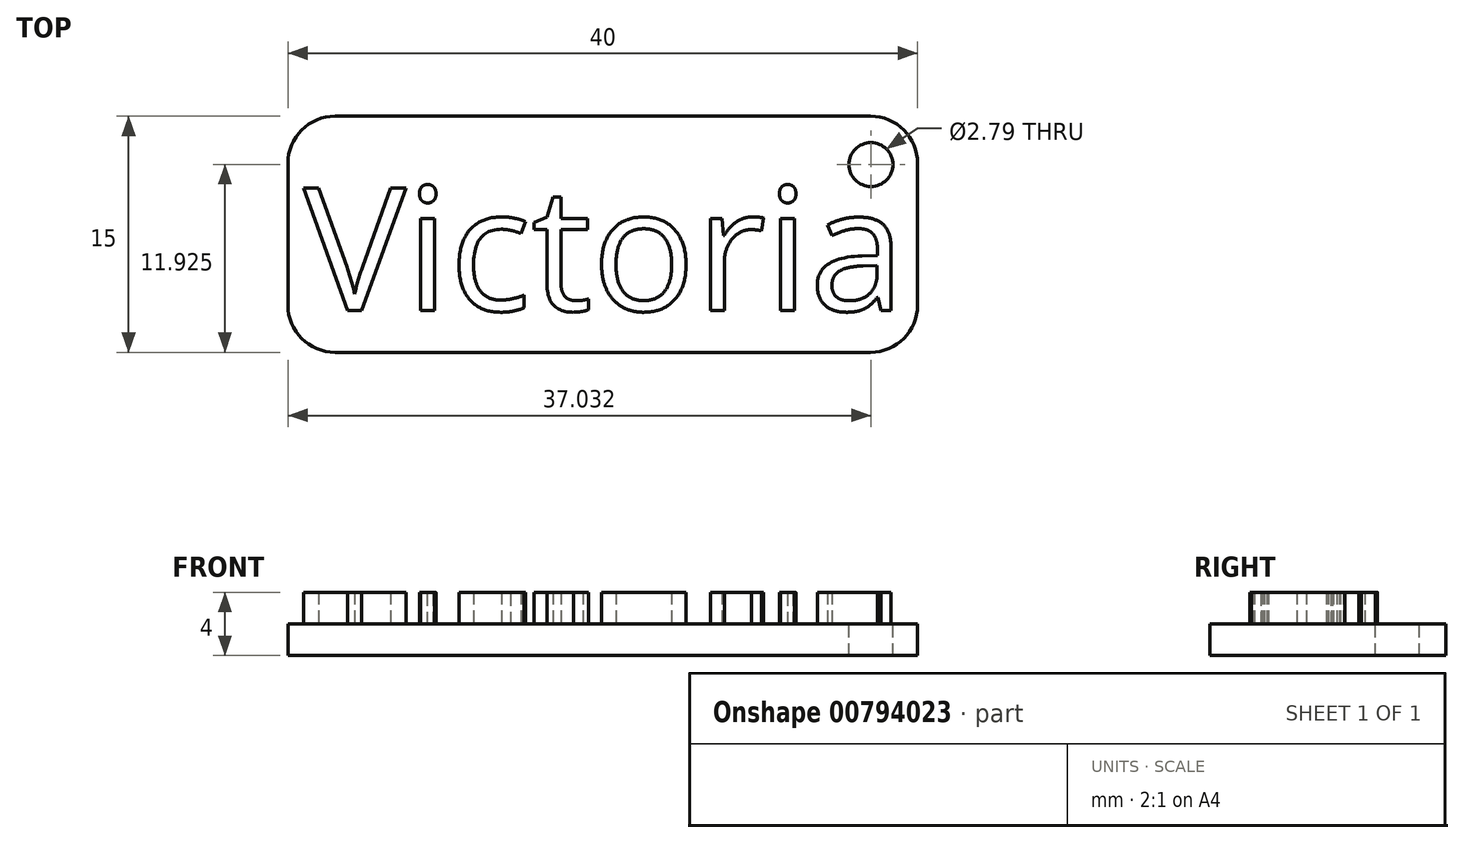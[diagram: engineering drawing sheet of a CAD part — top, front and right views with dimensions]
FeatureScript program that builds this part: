
annotation { "Feature Type Name" : "Feature", "Feature Type Description" : "" }
export const myFeature = defineFeature(function(context is Context, id is Id, definition is map)
    precondition{}
    {
        {
            var Q0;
            Q0=qCreatedBy(makeId("Top.planeOp"),FACE);
            var sketch = newSketch(context, id + "F0", { "sketchPlane" : qUnion([Q0])});
            skLineSegment(sketch, "E0.bottom", {"start": v(20, 7.5) * mm, "end": v(-20, 7.5) * mm});
            skLineSegment(sketch, "E0.top", {"start": v(20, -7.5) * mm, "end": v(-20, -7.5) * mm});
            skLineSegment(sketch, "E0.left", {"start": v(20, 7.5) * mm, "end": v(20, -7.5) * mm});
            skLineSegment(sketch, "E0.right", {"start": v(-20, 7.5) * mm, "end": v(-20, -7.5) * mm});
            skPoint(sketch, "E0.middle", {"position": v(0, 0) * mm});
            skSolve(sketch);
        }
        {
            var Q0;
            Q0=makeQuery(id+"F0.imprint","IMPRINT",FACE,{"disambiguationData":[TD([[makeQuery(id+"F0.imprint","IMPRINT",EDGE,{"derivedFrom":sQuery(id+"F0.wireOp",EDGE,"E0.bottom")}),1.0]])]});
            extrude(context, id + "F1", {"entities" : qUnion([Q0]), "depth" : 2 * mm, "offsetDistance" : 25 * mm});
        }
        {
            var Q0;
            Q0=makeQuery(id+"F1.opExtrude","CAP_FACE",FACE,{"disambiguationData":[OSD([sQuery(id+"F0.wireOp",EDGE,"E0.bottom"),sQuery(id+"F0.wireOp",EDGE,"E0.top"),sQuery(id+"F0.wireOp",EDGE,"E0.left"),sQuery(id+"F0.wireOp",EDGE,"E0.right")])],"isStart":false});
            var sketch = newSketch(context, id + "F2", { "sketchPlane" : qUnion([Q0])});
            skText(sketch, "E1", { "text": "Victoria", "fontName": "OpenSans-Regular.ttf"});
            const initialGuessF2  = {"E1": [-0.019, -0.00485, 1, 0, 0.00786]};
            skSetInitialGuess(sketch, initialGuessF2);
            skSolve(sketch);
        }
        {
            var Q0;
            Q0 = qSketchRegion(id + "F2", true);
            extrude(context, id + "F3", {"entities" : qUnion([Q0]), "operationType" : NewBodyOperationType.ADD, "depth" : 2 * mm, "offsetDistance" : 25 * mm});
        }
        {
            var Q0;
            Q0=makeQuery(id+"F1.opExtrude","SWEPT_EDGE",EDGE,{"disambiguationData":[OSD([sQuery(id+"F0.wireOp",EDGE,"E0.top"),sQuery(id+"F0.wireOp",EDGE,"E0.left")])]});
            var Q1;
            Q1=makeQuery(id+"F1.opExtrude","SWEPT_EDGE",EDGE,{"disambiguationData":[OSD([sQuery(id+"F0.wireOp",EDGE,"E0.bottom"),sQuery(id+"F0.wireOp",EDGE,"E0.left")])]});
            var Q2;
            Q2=makeQuery(id+"F1.opExtrude","SWEPT_EDGE",EDGE,{"disambiguationData":[OSD([sQuery(id+"F0.wireOp",EDGE,"E0.top"),sQuery(id+"F0.wireOp",EDGE,"E0.right")])]});
            var Q3;
            Q3=makeQuery(id+"F1.opExtrude","SWEPT_EDGE",EDGE,{"disambiguationData":[OSD([sQuery(id+"F0.wireOp",EDGE,"E0.bottom"),sQuery(id+"F0.wireOp",EDGE,"E0.right")])]});
            fillet(context, id + "F4", {"entities" : qUnion([Q0, Q1, Q2, Q3]), "radius" : 3 * mm, "tangentPropagation" : true, "allowEdgeOverflow" : false});
        }
        {
            var Q0;
            {var subQ0=sQuery(id+"F0.wireOp",EDGE,"E0.top");var subQ1=sQuery(id+"F0.wireOp",EDGE,"E0.right");var subQ2=sQuery(id+"F0.wireOp",EDGE,"E0.bottom");var subQ3=sQuery(id+"F0.wireOp",EDGE,"E0.left");Q0=makeQuery(id+"F3.boolean.opBoolean","SPLIT",FACE,{"disambiguationData":[TD([makeQuery(id+"F1.opExtrude","SWEPT_FACE",FACE,{"disambiguationData":[OSD([subQ2])]})])],"derivedFrom":makeQuery(id+"F1.opExtrude","CAP_FACE",FACE,{"disambiguationData":[OSD([subQ2,subQ0,subQ3,subQ1])],"isStart":false})});}
            var sketch = newSketch(context, id + "F5", { "sketchPlane" : qUnion([Q0])});
            skSolve(sketch);
        }
        {
            var Q0;
            {var subQ65=sQuery(id+"F2.wireOp",EDGE,"E1.sketch_text.stroke-0");Q0=makeQuery(id+"F5.imprint","IMPRINT",FACE,{"disambiguationData":[TD([[makeQuery(id+"F5.imprint","IMPRINT",EDGE,{"derivedFrom":makeQuery(id+"F3.opExtrude","CAP_EDGE",EDGE,{"disambiguationData":[OSD([subQ65])],"isStart":true})}),1.0]])]});}
            var sketch = newSketch(context, id + "F6", { "sketchPlane" : qUnion([Q0])});
            skCircle(sketch, "E2", {"center": v(17.03, 4.43) * mm, "radius": 1.4 * mm});
            skPoint(sketch, "E2.first.point", {"position": v(17.3, 5.8) * mm});
            skPoint(sketch, "E2.second.point", {"position": v(16.6, 3.1) * mm});
            skPoint(sketch, "E2.third.point", {"position": v(16.03, 3.45) * mm});
            skSolve(sketch);
        }
        {
            var Q0;
            Q0=makeQuery(id+"F6.imprint","IMPRINT",FACE,{"disambiguationData":[TD([[makeQuery(id+"F6.imprint","IMPRINT",EDGE,{"derivedFrom":sQuery(id+"F6.wireOp",EDGE,"E2")}),1.0]])]});
            extrude(context, id + "F7", {"entities" : qUnion([Q0]), "operationType" : NewBodyOperationType.REMOVE, "endBound" : BoundingType.THROUGH_ALL, "oppositeDirection" : true, "depth" : 25 * mm, "offsetDistance" : 25 * mm});
        }
    });
